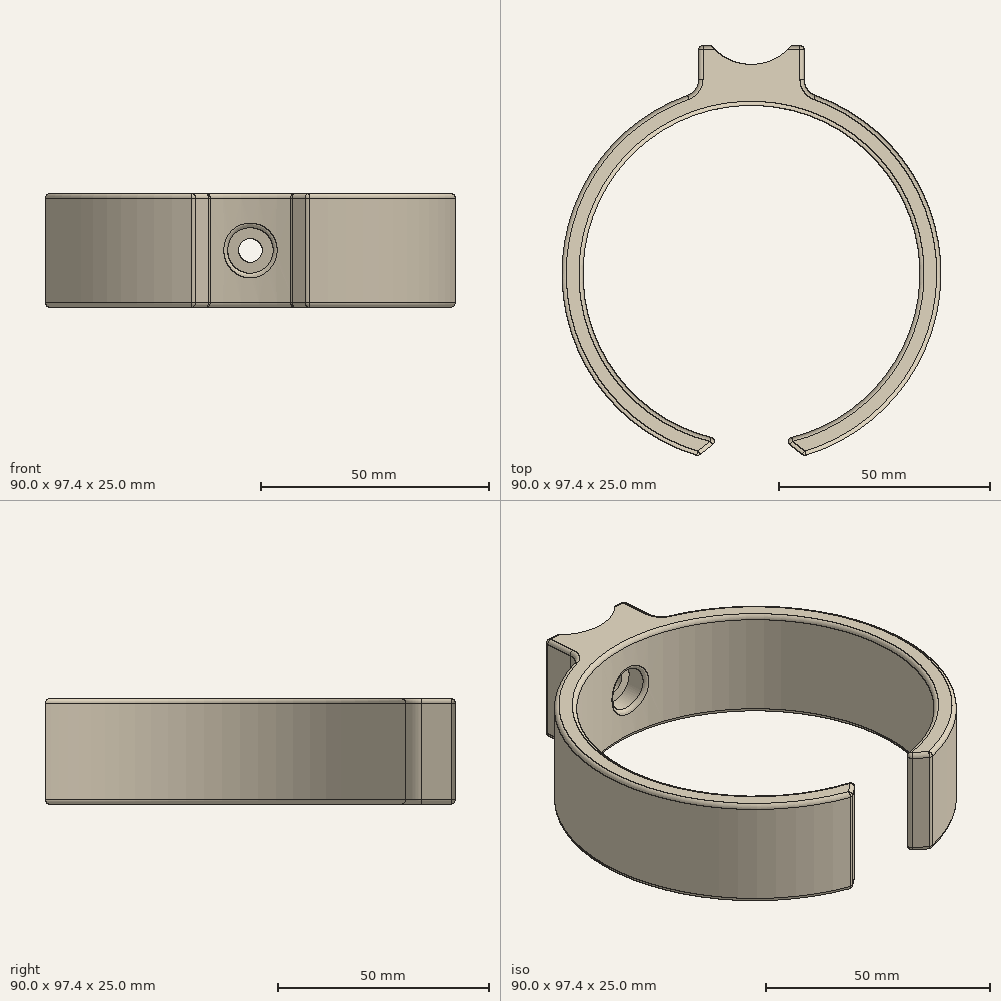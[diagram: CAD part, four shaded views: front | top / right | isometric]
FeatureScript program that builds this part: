
annotation { "Feature Type Name" : "Feature", "Feature Type Description" : "" }
export const myFeature = defineFeature(function(context is Context, id is Id, definition is map)
    precondition{}
    {
        {
            var Q0;
            Q0=qCreatedBy(makeId("Top.planeOp"),FACE);
            var sketch = newSketch(context, id + "F0", { "sketchPlane" : qUnion([Q0])});
            skArc(sketch, "E0", {"start": v(7.5, -24.41) * mm, "mid": v(0, 54.88) * mm, "end": v(-7.5, -24.41) * mm});
            skArc(sketch, "E1.0", {"start": v(12.5, -28.35) * mm, "mid": v(0, 59.88) * mm, "end": v(-12.5, -28.35) * mm});
            skLineSegment(sketch, "E2", {"start": v(12.5, 69.1) * mm, "end": v(-12.5, 69.1) * mm});
            skLineSegment(sketch, "E3", {"start": v(-12.5, 58.1) * mm, "end": v(-12.5, 69.1) * mm});
            skLineSegment(sketch, "E4", {"start": v(12.5, 69.1) * mm, "end": v(12.5, 58.1) * mm});
            skLineSegment(sketch, "E5", {"start": v(-7.5, -24.41) * mm, "end": v(-12.5, -28.35) * mm});
            skLineSegment(sketch, "E6", {"start": v(7.5, -24.41) * mm, "end": v(12.5, -28.35) * mm});
            skPoint(sketch, "E7", {"position": v(0, 69.1) * mm});
            skPoint(sketch, "E8", {"position": v(0, 77.1) * mm});
            skSolve(sketch);
        }
        {
            var Q0;
            Q0 = qSketchRegion(id + "F0", true);
            extrude(context, id + "F1", {"entities" : qUnion([Q0]), "depth" : 25 * mm});
        }
        {
            var Q0;
            Q0=makeQuery(id+"F1.opExtrude","SWEPT_EDGE",EDGE,{"disambiguationData":[OSD([sQuery(id+"F0.wireOp",EDGE,"E1.0"),sQuery(id+"F0.wireOp",EDGE,"E3")])]});
            fillet(context, id + "F2", {"entities" : qUnion([Q0]), "radius" : 4 * mm, "tangentPropagation" : true, "allowEdgeOverflow" : false});
        }
        {
            var Q0;
            Q0=makeQuery(id+"F1.opExtrude","SWEPT_EDGE",EDGE,{"disambiguationData":[OSD([sQuery(id+"F0.wireOp",EDGE,"E1.0"),sQuery(id+"F0.wireOp",EDGE,"E4")])]});
            fillet(context, id + "F3", {"entities" : qUnion([Q0]), "radius" : 4 * mm, "tangentPropagation" : true, "allowEdgeOverflow" : false});
        }
        {
            var Q0;
            Q0=makeQuery(id+"F1.opExtrude","SWEPT_EDGE",EDGE,{"disambiguationData":[OSD([sQuery(id+"F0.wireOp",EDGE,"E0"),sQuery(id+"F0.wireOp",EDGE,"E6")])]});
            var Q1;
            Q1=makeQuery(id+"F1.opExtrude","SWEPT_EDGE",EDGE,{"disambiguationData":[OSD([sQuery(id+"F0.wireOp",EDGE,"E1.0"),sQuery(id+"F0.wireOp",EDGE,"E6")])]});
            var Q2;
            Q2=makeQuery(id+"F1.opExtrude","SWEPT_EDGE",EDGE,{"disambiguationData":[OSD([sQuery(id+"F0.wireOp",EDGE,"E0"),sQuery(id+"F0.wireOp",EDGE,"E5")])]});
            var Q3;
            Q3=makeQuery(id+"F1.opExtrude","SWEPT_EDGE",EDGE,{"disambiguationData":[OSD([sQuery(id+"F0.wireOp",EDGE,"E1.0"),sQuery(id+"F0.wireOp",EDGE,"E5")])]});
            var Q4;
            Q4=makeQuery(id+"F1.opExtrude","SWEPT_EDGE",EDGE,{"disambiguationData":[OSD([sQuery(id+"F0.wireOp",EDGE,"E2"),sQuery(id+"F0.wireOp",EDGE,"E4")])]});
            var Q5;
            Q5=makeQuery(id+"F1.opExtrude","SWEPT_EDGE",EDGE,{"disambiguationData":[OSD([sQuery(id+"F0.wireOp",EDGE,"E2"),sQuery(id+"F0.wireOp",EDGE,"E3")])]});
            fillet(context, id + "F4", {"entities" : qUnion([Q0, Q1, Q2, Q3, Q4, Q5]), "radius" : 1 * mm, "tangentPropagation" : true, "allowEdgeOverflow" : false});
        }
        {
            var Q0;
            Q0=qCreatedBy(makeId("Front.planeOp"),FACE);
            var sketch = newSketch(context, id + "F5", { "sketchPlane" : qUnion([Q0])});
            skLineSegment(sketch, "E9.0", {"start": v(5, 25) * mm, "end": v(-5, 25) * mm});
            skLineSegment(sketch, "E10", {"start": v(-40, 0) * mm, "end": v(-40, 25) * mm});
            skLineSegment(sketch, "E11", {"start": v(40, 25) * mm, "end": v(40, 0) * mm});
            skLineSegment(sketch, "E12", {"start": v(45, 25) * mm, "end": v(45, 0) * mm});
            skLineSegment(sketch, "E13", {"start": v(-45, 0) * mm, "end": v(-45, 25) * mm});
            skLineSegment(sketch, "E14.0.0", {"start": v(5, 0) * mm, "end": v(-5, 0) * mm});
            skLineSegment(sketch, "E14.0.1", {"start": v(-5, 0) * mm, "end": v(-5, 25) * mm});
            skLineSegment(sketch, "E14.0.2", {"start": v(-5, 25) * mm, "end": v(5, 25) * mm});
            skLineSegment(sketch, "E14.0.3", {"start": v(5, 25) * mm, "end": v(5, 0) * mm});
            skPoint(sketch, "E15.0", {"position": v(0, 0) * mm});
            skPoint(sketch, "E16", {"position": v(0, 12.5) * mm});
            skPoint(sketch, "E16.positionSnap0", {"position": v(0, 25) * mm});
            skSolve(sketch);
        }
        {
            var Q0;
            Q0=sQuery(id+"F5.wireOp",VERTEX,"E16");
            var Q1;
            Q1=makeQuery(id+"F1.opExtrude","SWEPT_BODY",BODY,{"disambiguationData":[OSD([sQuery(id+"F0.wireOp",EDGE,"E0"),sQuery(id+"F0.wireOp",EDGE,"E1.0"),sQuery(id+"F0.wireOp",EDGE,"E2"),sQuery(id+"F0.wireOp",EDGE,"E3"),sQuery(id+"F0.wireOp",EDGE,"E4"),sQuery(id+"F0.wireOp",EDGE,"E5"),sQuery(id+"F0.wireOp",EDGE,"E6")])]});
            hole(context, id + "F6", {"style" : HoleStyle.C_BORE, "endStyle" : HoleEndStyle.THROUGH, "holeDiameter" : 5.2 * mm, "cBoreDiameter" : 10 * mm, "cBoreDepth" : 5 * mm, "majorDiameter" : 5 * mm, "tappedDepth" : 12 * mm, "tapClearance" : 3, "locations" : qUnion([Q0]), "scope" : qUnion([Q1]), "startStyle" : HoleStartStyle.PART});
        }
        {
            var Q0;
            Q0=makeQuery(id+"F6.hole-0.boolean.opBoolean","COPY",EDGE,{"derivedFrom":makeQuery(id+"F6.hole-0.opRevolve","SWEPT_EDGE",EDGE,{"disambiguationData":[OSD([sQuery(id+"F6.hole-0.sketch.wireOp",EDGE,"cbore_start_line_1"),sQuery(id+"F6.hole-0.sketch.wireOp",EDGE,"cbore_start_line_2")])]})});
            var Q1;
            Q1=makeQuery(id+"F1.opExtrude","SWEPT_FACE",FACE,{"disambiguationData":[OSD([sQuery(id+"F0.wireOp",EDGE,"E0")])]});
            fillet(context, id + "F7", {"entities" : qUnion([Q0, Q1]), "radius" : 1 * mm, "tangentPropagation" : true, "allowEdgeOverflow" : false});
        }
        {
            var Q0;
            Q0=sQuery(id+"F0.wireOp",VERTEX,"E8");
            var Q1;
            Q1=makeQuery(id+"F1.opExtrude","SWEPT_BODY",BODY,{"disambiguationData":[OSD([sQuery(id+"F0.wireOp",EDGE,"E0"),sQuery(id+"F0.wireOp",EDGE,"E1.0"),sQuery(id+"F0.wireOp",EDGE,"E2"),sQuery(id+"F0.wireOp",EDGE,"E3"),sQuery(id+"F0.wireOp",EDGE,"E4"),sQuery(id+"F0.wireOp",EDGE,"E5"),sQuery(id+"F0.wireOp",EDGE,"E6")])]});
            hole(context, id + "F8", {"style" : HoleStyle.SIMPLE, "endStyle" : HoleEndStyle.THROUGH, "oppositeDirection" : true, "holeDiameter" : 25 * mm, "majorDiameter" : 5 * mm, "tappedDepth" : 12 * mm, "tapClearance" : 3, "locations" : qUnion([Q0]), "scope" : qUnion([Q1]), "startStyle" : HoleStartStyle.PART});
        }
        {
            var Q0;
            {var subQ0=sQuery(id+"F0.wireOp",EDGE,"E2");var subQ3=sQuery(id+"F0.wireOp",EDGE,"E4");Q0=makeQuery(id+"F8.hole-0.boolean.opBoolean","SPLIT",FACE,{"disambiguationData":[TD([makeQuery(id+"F4.opFillet","BLEND_FACE",FACE,{"disambiguationData":[OSD([subQ0,subQ3])]})])],"derivedFrom":makeQuery(id+"F1.opExtrude","SWEPT_FACE",FACE,{"disambiguationData":[OSD([subQ0])]})});}
            var sketch = newSketch(context, id + "F9", { "sketchPlane" : qUnion([Q0])});
            skLineSegment(sketch, "E17.0.0", {"start": v(-8.67, 0) * mm, "end": v(8.67, 0) * mm});
            skFitSpline(sketch, "E17.0.1", {"points": [v(8.67, 0) * mm, v(8.79, 0) * mm, v(9, 0.04) * mm, v(9.3, 0.2) * mm, v(9.54, 0.53) * mm, v(9.6, 0.84) * mm, v(9.6, 1) * mm]});
            skLineSegment(sketch, "E17.0.2", {"start": v(9.6, 1) * mm, "end": v(9.6, 24) * mm});
            skFitSpline(sketch, "E17.0.3", {"points": [v(9.6, 24) * mm, v(9.6, 24.16) * mm, v(9.54, 24.47) * mm, v(9.3, 24.8) * mm, v(9, 24.97) * mm, v(8.79, 25) * mm, v(8.67, 25) * mm]});
            skLineSegment(sketch, "E17.0.4", {"start": v(-8.67, 25) * mm, "end": v(8.67, 25) * mm});
            skFitSpline(sketch, "E17.0.5", {"points": [v(-8.67, 25) * mm, v(-8.79, 25) * mm, v(-9, 24.96) * mm, v(-9.3, 24.8) * mm, v(-9.54, 24.47) * mm, v(-9.6, 24.16) * mm, v(-9.6, 24) * mm]});
            skLineSegment(sketch, "E17.0.6", {"start": v(-9.6, 24) * mm, "end": v(-9.6, 1) * mm});
            skFitSpline(sketch, "E17.0.7", {"points": [v(-9.6, 1) * mm, v(-9.6, 0.84) * mm, v(-9.54, 0.53) * mm, v(-9.3, 0.2) * mm, v(-9, 0.03) * mm, v(-8.79, 0) * mm, v(-8.67, 0) * mm]});
            skCircle(sketch, "E18.0", {"center": v(0, 12.5) * mm, "radius": 2.6 * mm});
            skSolve(sketch);
        }
        {
            var Q0;
            Q0=sQuery(id+"F9.wireOp",VERTEX,"E18.0.center");
            var Q1;
            Q1=makeQuery(id+"F1.opExtrude","SWEPT_BODY",BODY,{"disambiguationData":[OSD([sQuery(id+"F0.wireOp",EDGE,"E0"),sQuery(id+"F0.wireOp",EDGE,"E1.0"),sQuery(id+"F0.wireOp",EDGE,"E2"),sQuery(id+"F0.wireOp",EDGE,"E3"),sQuery(id+"F0.wireOp",EDGE,"E4"),sQuery(id+"F0.wireOp",EDGE,"E5"),sQuery(id+"F0.wireOp",EDGE,"E6")])]});
            hole(context, id + "F10", {"style" : HoleStyle.C_BORE, "endStyle" : HoleEndStyle.BLIND, "holeDiameter" : 4 * mm, "cBoreDiameter" : 12 * mm, "cBoreDepth" : 1 * mm, "majorDiameter" : 5 * mm, "holeDepth" : 12 * mm, "tappedDepth" : 12 * mm, "tapClearance" : 3, "locations" : qUnion([Q0]), "scope" : qUnion([Q1]), "startStyle" : HoleStartStyle.PART});
        }
    });
